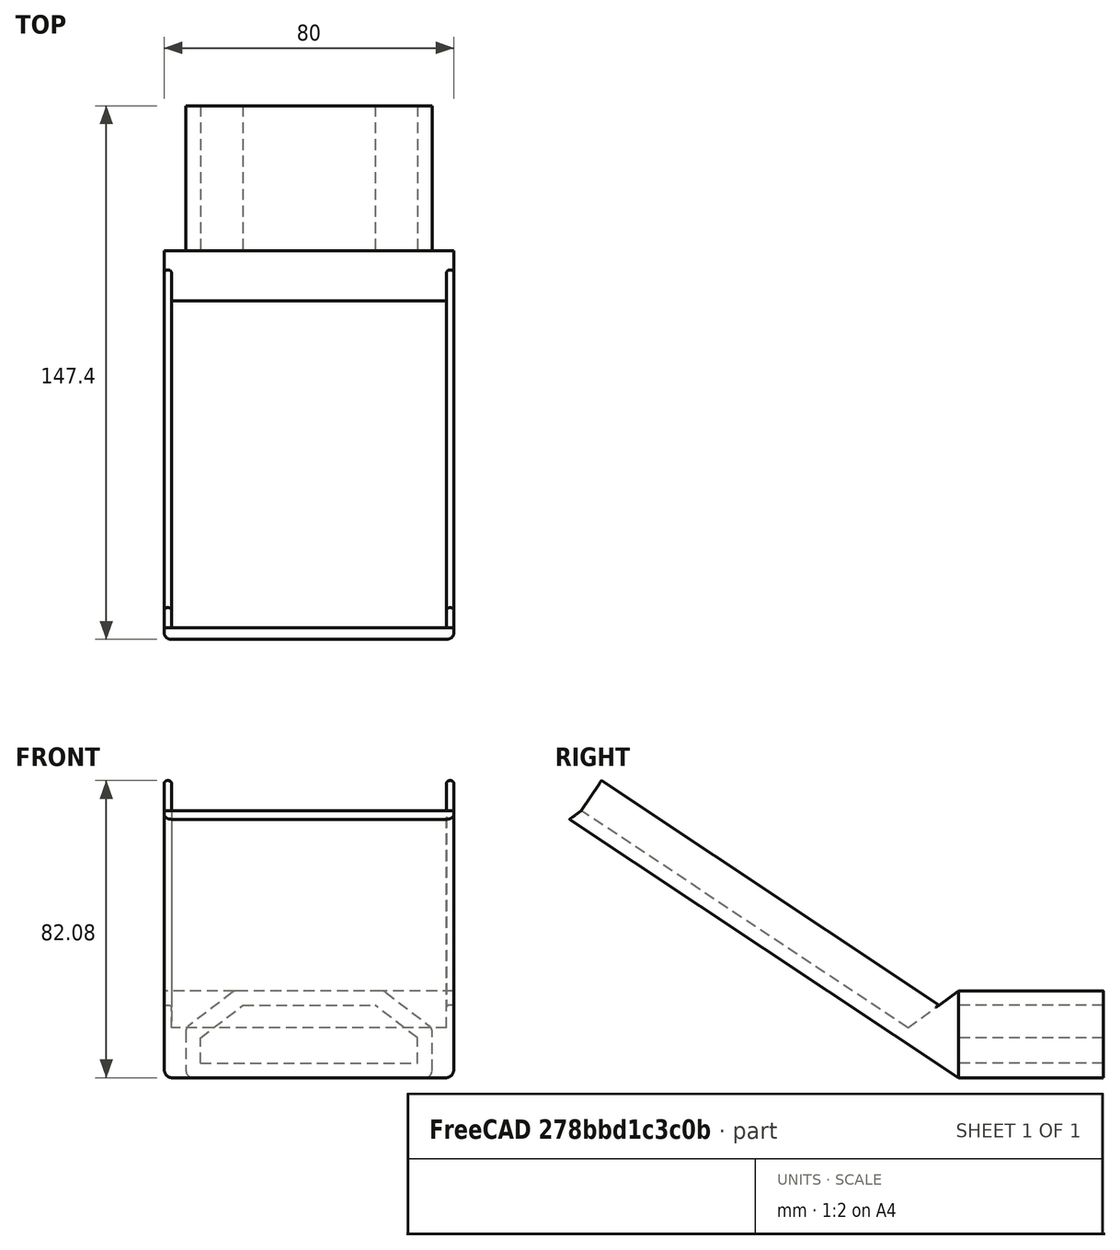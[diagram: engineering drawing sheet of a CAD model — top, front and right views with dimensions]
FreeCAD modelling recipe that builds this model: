
FCSTD DOCUMENT  (FreeCAD 1.0R39109 (Git))
Label: iPhoneSpinnerMount
License: All rights reserved
LicenseURL: https://en.wikipedia.org/wiki/All_rights_reserved
objects: PartDesign::Pad×4, Sketcher::SketchObject×3, PartDesign::Fillet×2, PartDesign::Body×1, Mesh::Feature×1
note: 25 computed .brp shape members not serialized (recipe doc carries the construction recipe); baked Part::Feature solids carry a one-line shape summary decoded from their .brp

FEATURE [Sketcher::SketchObject] Sketch
  ArcFitTolerance = 1e-06
  AttachmentSupport = -> [XZ_Plane]
  FullyConstrained = true
  MakeInternals = false
  MapMode = 5
  Placement = pos=(0,0,0) rot=(1,0,0;1.5708rad)
  expr: Constraints[32] = 1.13 * .Constraints.topWidth
  sketch-geometry (12):
    g0: LineSegment StartX=-30 StartY=0 StartZ=0 EndX=30 EndY=0 EndZ=0
    g1: LineSegment StartX=-30 StartY=0 StartZ=0 EndX=-30 EndY=7 EndZ=0
    g2: LineSegment StartX=30 StartY=0 StartZ=0 EndX=30 EndY=7 EndZ=0
    g3: LineSegment StartX=-18.25 StartY=16 StartZ=0 EndX=18.25 EndY=16 EndZ=0
    g4: LineSegment StartX=-30 StartY=7 StartZ=0 EndX=-18.25 EndY=16 EndZ=0
    g5: LineSegment StartX=30 StartY=7 StartZ=0 EndX=18.25 EndY=16 EndZ=0
    g6: LineSegment StartX=-20.6225 StartY=20 StartZ=0 EndX=-34 EndY=9.7534 EndZ=0
    g7: LineSegment StartX=20.6225 StartY=20 StartZ=0 EndX=34 EndY=9.7534 EndZ=0
    g8: LineSegment StartX=20.6225 StartY=20 StartZ=0 EndX=-20.6225 EndY=20 EndZ=0
    g9: LineSegment StartX=-34 StartY=9.7534 StartZ=0 EndX=-34 EndY=-4 EndZ=0
    g10: LineSegment StartX=-34 StartY=-4 StartZ=0 EndX=34 EndY=-4 EndZ=0
    g11: LineSegment StartX=34 StartY=-4 StartZ=0 EndX=34 EndY=9.7534 EndZ=0
  constraints (33):
    c: PointOnObject(g0,g-1)
    c: DistanceX(g0,g0) = 60  'width'
    c: Symmetric(g0,g0,g-1)
    c: Coincident(g1,g0)
    c: Vertical(g1)
    c: Coincident(g2,g0)
    c: Vertical(g2)
    c: DistanceY(g1,g1) = 7
    c: Equal(g1,g2)
    c: Symmetric(g3,g3,g-2)
    c: DistanceX(g3,g3) = 36.5  'topWidth'
    c: Coincident(g4,g1)
    c: Coincident(g4,g3)
    c: Coincident(g5,g2)
    c: Coincident(g5,g3)
    c: DistanceY(g-1,g3) = 16
    c: Coincident(g8,g7)
    c: Coincident(g8,g6)
    c: Coincident(g9,g6)
    c: Vertical(g9)
    c: Coincident(g10,g9)
    c: Horizontal(g10)
    c: Coincident(g11,g10)
    c: Coincident(g11,g7)
    c: Vertical(g11)
    c: Parallel(g6,g4)
    c: Parallel(g7,g5)
    c: DistanceX(g0,g10) = 4
    c: DistanceY(g10,g0) = 4
    c: DistanceX(g9,g0) = 4
    c: DistanceY(g3,g6) = 4
    c: Symmetric(g6,g7,g-2)
    c: DistanceX(g8,g8) = 41.245
FEATURE [PartDesign::Pad] Pad
  Direction = (0,-1,2e-16)
  Length = 40
  Length2 = 10
  Placement = pos=(0,0,0) rot=(1,0,0;1.5708rad)
  Profile = -> Sketch
  ReferenceAxis = -> Sketch [N_Axis]
  Refine = true
  Suppressed = false
  Type = 0
FEATURE [Sketcher::SketchObject] Sketch002
  ArcFitTolerance = 1e-06
  AttachmentOffset = pos=(0,0,-34) rot=(0,0,1;0rad)
  AttachmentSupport = -> [Pad]
  ExternalGeometry = -> [Pad]
  FullyConstrained = true
  MakeInternals = false
  MapMode = 5
  Placement = pos=(0,0,7.5e-15) rot=(0.707107,0,-0.707107;3.14159rad)
  sketch-geometry (5):
    g0: LineSegment StartX=4 StartY=40 StartZ=0 EndX=-67.3802 EndY=147.399 EndZ=0
    g1: LineSegment StartX=4 StartY=40 StartZ=0 EndX=-20 EndY=40 EndZ=0
    g2: LineSegment StartX=-20 StartY=40 StartZ=0 EndX=-9.7534 EndY=53.9028 EndZ=0
    g3: LineSegment StartX=-9.7534 StartY=53.9028 StartZ=0 EndX=-69.7534 EndY=144.179 EndZ=0
    g4: LineSegment StartX=-69.7534 StartY=144.179 StartZ=0 EndX=-67.3802 EndY=147.399 EndZ=0
  constraints (13):
    c: Coincident(g0,g-3)
    c: Coincident(g1,g0)
    c: Coincident(g1,g-4)
    c: Coincident(g2,g1)
    c: Coincident(g3,g2)
    c: Coincident(g0,g4)
    c: Parallel(g3,g0)
    c: Coincident(g3,g4)
    c: Parallel(g2,g4)
    c: Vertical(g-3,g2)
    c: Angle(g3,g2) = 1.91986
    c: Distance(g3,g0) = 4
    c: DistanceX(g3,g3) = 60
FEATURE [PartDesign::Pad] Pad001
  BaseFeature = -> Pad
  Direction = (-1,0,-2e-16)
  Length = 80
  Length2 = 10
  Midplane = true
  Placement = pos=(0,0,0) rot=(1,0,0;1.5708rad)
  Profile = -> Sketch002
  ReferenceAxis = -> Sketch002 [N_Axis]
  Refine = true
  Suppressed = false
  Type = 0
FEATURE [Sketcher::SketchObject] Sketch003
  ArcFitTolerance = 1e-06
  AttachmentSupport = -> [Pad001]
  ExternalGeometry = -> [Pad001]
  FullyConstrained = true
  MakeInternals = false
  MapMode = 5
  Placement = pos=(4e-15,-12.019,-18.0837) rot=(0,0.289108,0.957296;3.14159rad)
  sketch-geometry (8):
    g0: LineSegment StartX=-40 StartY=50.2908 StartZ=0 EndX=-38 EndY=50.2908 EndZ=0
    g1: LineSegment StartX=-38 StartY=50.2908 StartZ=0 EndX=-38 EndY=158.687 EndZ=0
    g2: LineSegment StartX=-38 StartY=158.687 StartZ=0 EndX=-40 EndY=158.687 EndZ=0
    g3: LineSegment StartX=-40 StartY=158.687 StartZ=0 EndX=-40 EndY=50.2908 EndZ=0
    g4: LineSegment StartX=40 StartY=50.2908 StartZ=0 EndX=40 EndY=158.687 EndZ=0
    g5: LineSegment StartX=40 StartY=158.687 StartZ=0 EndX=38 EndY=158.687 EndZ=0
    g6: LineSegment StartX=38 StartY=158.687 StartZ=0 EndX=38 EndY=50.2908 EndZ=0
    g7: LineSegment StartX=38 StartY=50.2908 StartZ=0 EndX=40 EndY=50.2908 EndZ=0
  constraints (22):
    c: Coincident(g0,g1)
    c: Coincident(g1,g2)
    c: Coincident(g2,g3)
    c: Coincident(g3,g0)
    c: Horizontal(g0)
    c: Horizontal(g2)
    c: Vertical(g1)
    c: Vertical(g3)
    c: Coincident(g0,g-3)
    c: Coincident(g4,g5)
    c: Coincident(g5,g6)
    c: Coincident(g6,g7)
    c: Coincident(g7,g4)
    c: Vertical(g4)
    c: Vertical(g6)
    c: Horizontal(g5)
    c: Horizontal(g7)
    c: Coincident(g4,g-4)
    c: DistanceX(g2,g2) = 2
    c: DistanceX(g5,g5) = 2
    c: Horizontal(g-3,g1)
    c: Horizontal(g1,g5)
FEATURE [PartDesign::Pad] Pad002
  BaseFeature = -> Pad001
  Direction = (0,0.553524,0.832833)
  Length = 10
  Length2 = 10
  Placement = pos=(0,0,0) rot=(1,0,0;1.5708rad)
  Profile = -> Sketch003
  ReferenceAxis = -> Sketch003 [N_Axis]
  Refine = true
  Suppressed = false
  Type = 0
FEATURE [PartDesign::Pad] Pad003
  BaseFeature = -> Pad002
  Direction = (0,0.832833,-0.553524)
  Length = 10
  Length2 = 10
  Placement = pos=(0,0,0) rot=(1,0,0;1.5708rad)
  Profile = -> Pad002 [Face19,Face17]
  Refine = true
  Suppressed = false
  Type = 0
FEATURE [PartDesign::Fillet] Fillet
  Base = -> Pad003 [Edge5,Edge29,Edge1,Edge2,Edge8,Edge33,Edge55,Edge54]
  BaseFeature = -> Pad003
  Placement = pos=(0,0,0) rot=(1,0,0;1.5708rad)
  Radius = 2
  Refine = true
  SupportTransform = false
  Suppressed = false
  UseAllEdges = false
FEATURE [PartDesign::Fillet] Fillet001
  Base = -> Fillet [Edge76,Edge82,Edge85,Edge80]
  BaseFeature = -> Fillet
  Placement = pos=(0,0,0) rot=(1,0,0;1.5708rad)
  Radius = 0.95
  Refine = true
  SupportTransform = false
  Suppressed = false
  UseAllEdges = false
FEATURE [PartDesign::Body] Body
  AllowCompound = false
  Group = -> [Sketch,Pad,Sketch002,Pad001,Sketch003,Pad002,Pad003,Fillet,Fillet001]
  Origin = -> Origin
  Tip = -> Fillet001
FEATURE [Mesh::Feature] Mesh  label="Fillet001 (Meshed)"
